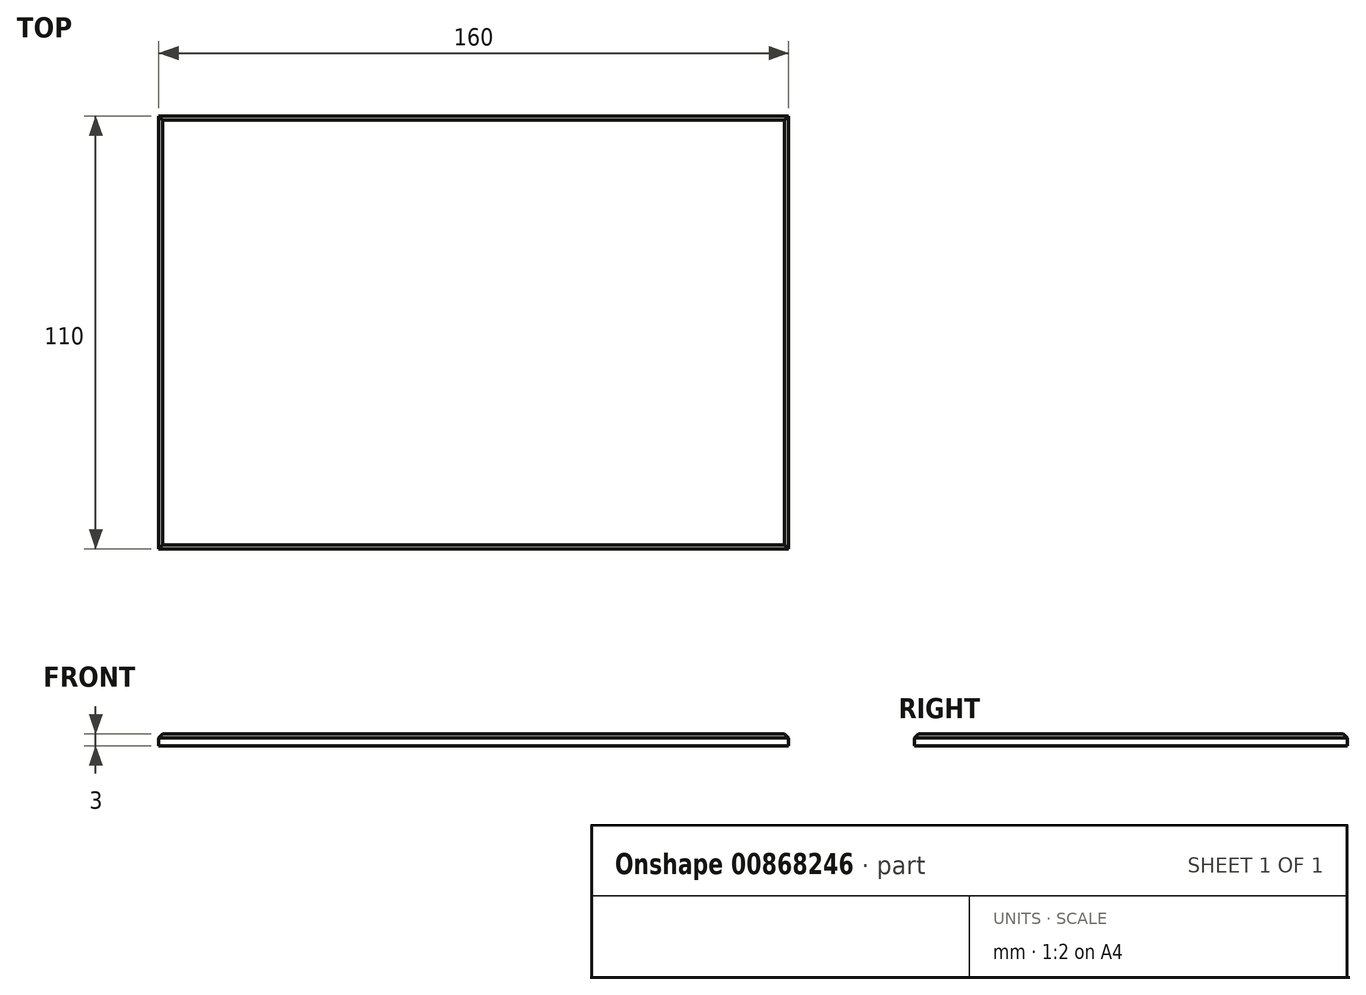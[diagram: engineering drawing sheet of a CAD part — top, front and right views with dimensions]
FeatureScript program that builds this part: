
annotation { "Feature Type Name" : "Feature", "Feature Type Description" : "" }
export const myFeature = defineFeature(function(context is Context, id is Id, definition is map)
    precondition{}
    {
        {
            var Q0;
            Q0=qCreatedBy(makeId("Top.planeOp"),FACE);
            var sketch = newSketch(context, id + "F0", { "sketchPlane" : qUnion([Q0])});
            skLineSegment(sketch, "E0.bottom", {"start": v(80, 55) * mm, "end": v(-80, 55) * mm});
            skLineSegment(sketch, "E0.top", {"start": v(80, -55) * mm, "end": v(-80, -55) * mm});
            skLineSegment(sketch, "E0.left", {"start": v(80, 55) * mm, "end": v(80, -55) * mm});
            skLineSegment(sketch, "E0.right", {"start": v(-80, 55) * mm, "end": v(-80, -55) * mm});
            skPoint(sketch, "E0.middle", {"position": v(0, 0) * mm});
            skSolve(sketch);
        }
        {
            var Q0;
            Q0 = qSketchRegion(id + "F0", true);
            extrude(context, id + "F1", {"entities" : qUnion([Q0]), "depth" : 3 * mm, "offsetDistance" : 25.4 * mm});
        }
        {
            var Q0;
            Q0=makeQuery(id+"F1.opExtrude","CAP_EDGE",EDGE,{"disambiguationData":[OSD([sQuery(id+"F0.wireOp",EDGE,"E0.right")])],"isStart":false});
            var Q1;
            Q1=makeQuery(id+"F1.opExtrude","CAP_EDGE",EDGE,{"disambiguationData":[OSD([sQuery(id+"F0.wireOp",EDGE,"E0.top")])],"isStart":false});
            var Q2;
            Q2=makeQuery(id+"F1.opExtrude","CAP_EDGE",EDGE,{"disambiguationData":[OSD([sQuery(id+"F0.wireOp",EDGE,"E0.left")])],"isStart":false});
            var Q3;
            Q3=makeQuery(id+"F1.opExtrude","CAP_EDGE",EDGE,{"disambiguationData":[OSD([sQuery(id+"F0.wireOp",EDGE,"E0.bottom")])],"isStart":false});
            chamfer(context, id + "F2", {"entities" : qUnion([Q0, Q1, Q2, Q3]), "width" : 1 * mm, "tangentPropagation" : true});
        }
    });
